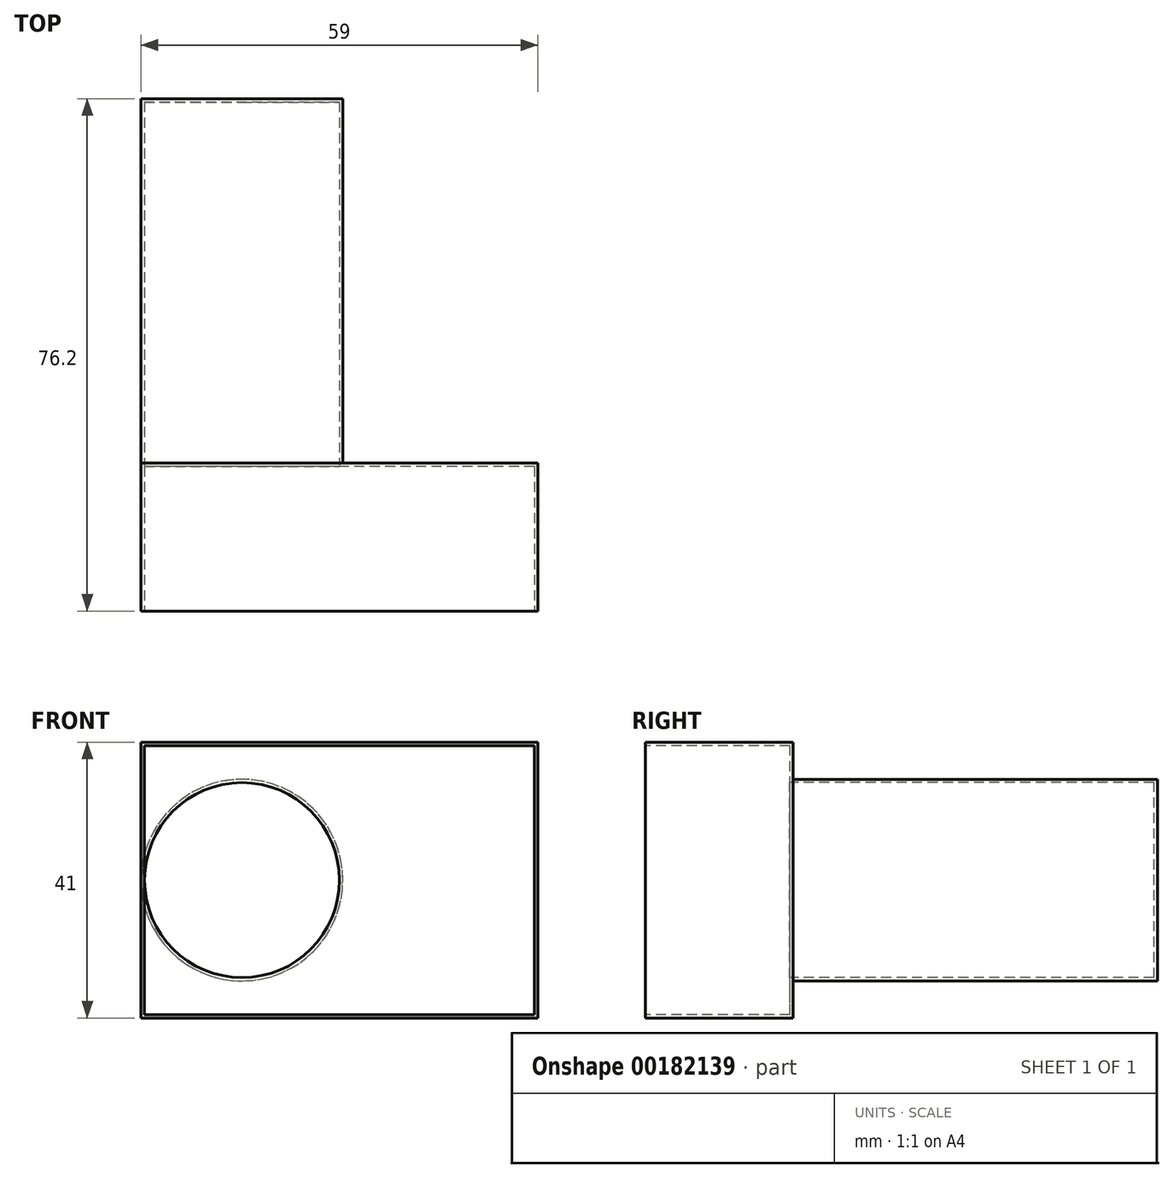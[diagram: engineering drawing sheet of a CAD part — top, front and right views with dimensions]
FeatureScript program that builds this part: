
annotation { "Feature Type Name" : "Feature", "Feature Type Description" : "" }
export const myFeature = defineFeature(function(context is Context, id is Id, definition is map)
    precondition{}
    {
        {
            var Q0;
            Q0=qCreatedBy(makeId("Front.planeOp"),FACE);
            var sketch = newSketch(context, id + "F0", { "sketchPlane" : qUnion([Q0])});
            skLineSegment(sketch, "E0.bottom", {"start": v(29.5, 20.5) * mm, "end": v(-29.5, 20.5) * mm});
            skLineSegment(sketch, "E0.top", {"start": v(29.5, -20.5) * mm, "end": v(-29.5, -20.5) * mm});
            skLineSegment(sketch, "E0.left", {"start": v(29.5, 20.5) * mm, "end": v(29.5, -20.5) * mm});
            skLineSegment(sketch, "E0.right", {"start": v(-29.5, 20.5) * mm, "end": v(-29.5, -20.5) * mm});
            skPoint(sketch, "E0.middle", {"position": v(0, 0) * mm});
            skSolve(sketch);
        }
        {
            var Q0;
            Q0 = qSketchRegion(id + "F0", true);
            extrude(context, id + "F1", {"entities" : qUnion([Q0]), "oppositeDirection" : true, "depth" : 22 * mm});
        }
        {
            var Q0;
            Q0=qCreatedBy(makeId("Front.planeOp"),FACE);
            var sketch = newSketch(context, id + "F2", { "sketchPlane" : qUnion([Q0])});
            skLineSegment(sketch, "E1", {"start": v(-92.03, 0) * mm, "end": v(97.37, 0) * mm, "construction": true});
            skLineSegment(sketch, "E2", {"start": v(0, 48.69) * mm, "end": v(0, -65.47) * mm, "construction": true});
            skCircle(sketch, "E3", {"center": v(-14.5, 0) * mm, "radius": 15 * mm});
            skSolve(sketch);
        }
        {
            var Q0;
            Q0 = qSketchRegion(id + "F2", true);
            extrude(context, id + "F3", {"entities" : qUnion([Q0]), "operationType" : NewBodyOperationType.ADD, "oppositeDirection" : true, "depth" : 76.2 * mm});
        }
        {
            var Q0;
            Q0=makeQuery(id+"F1.opExtrude","CAP_FACE",FACE,{"disambiguationData":[OSD([sQuery(id+"F0.wireOp",EDGE,"E0.bottom"),sQuery(id+"F0.wireOp",EDGE,"E0.top"),sQuery(id+"F0.wireOp",EDGE,"E0.left"),sQuery(id+"F0.wireOp",EDGE,"E0.right")])],"isStart":true});
            shell(context, id + "F4", {"entities" : qUnion([Q0]), "thickness" : 0.5 * mm});
        }
    });
